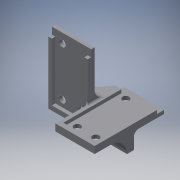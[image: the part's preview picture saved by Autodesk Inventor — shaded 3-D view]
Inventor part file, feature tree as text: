
AUTODESK INVENTOR PART (.ipt)
format: ipt  version: 2016 (Build 200138000, 138)  size: 277,504 bytes
history: native  units: mm
features: extrude x11, sketch x10, projected_geometry x10, fillet x7
ambient origin geometry x8: Origin, YZ Plane, XZ Plane, XY Plane, X Axis, Y Axis, Z Axis, Center Point
bodies: Solid1 (feature_tree)
feature tree (38):
  extrude  "Extrusion1"  Depth=13.0mm
  extrude  "Extrusion4"  Depth=17.0mm
  extrude  "Extrusion8"  Depth=30.0mm TaperAngle=0.0deg
  extrude  "Extrusion14"  Depth=20.0mm TaperAngle=0.0deg
  extrude  "Extrusion15"  Depth=21.0mm
  extrude  "Extrusion16"  Depth=8.0mm
  extrude  "Extrusion18"  Depth=2.8mm
  extrude  "Extrusion19"  Depth=8.0mm
  fillet  "Fillet6"  Radius=3.0mm
  fillet  "Fillet7"  Radius=3.0mm
  fillet  "Fillet8"  Radius=1.5mm
  fillet  "Fillet9"  Radius=1.5mm
  fillet  "Fillet10"  Radius=1.5mm
  fillet  "Fillet11"  Radius=0.6mm
  sketch  "Sketch11"  dims[d22=7.0mm d23=0.0mm d42=20.0mm d43=0.0mm]
  sketch  "Sketch12"  dims[d54=2.7mm d55=21.0mm]
  extrude  "Extrusion11"  Depth=1.5mm
  extrude  "Extrusion12"  Depth=1.0mm
  extrude  "Extrusion13"  Depth=1.0mm
  fillet  "Fillet5"  Radius=1.5mm
  sketch  "Sketch1"  dims[d0=17.0mm d1=13.0mm]
  sketch  "Sketch4"  dims[d2=17.0mm d4=17.0mm]
  projected_geometry  "Projected Loop3"
  sketch  "Sketch8"  dims[d5=14.0mm d6=30.0mm d7=0.0mm]
  projected_geometry  "Projected Loop7"
  projected_geometry  "Projected Loop8"
  projected_geometry  "Projected Loop10"
  projected_geometry  "Projected Loop11"
  sketch  "Sketch13"  dims[d56=3.0mm d57=8.0mm]
  projected_geometry  "Projected Loop12"
  sketch  "Sketch14"  dims[d58=3.0mm d59=2.8mm]
  projected_geometry  "Projected Loop13"
  sketch  "Sketch15"  dims[d60=21.0mm d61=8.0mm d62=3.0mm d63=3.0mm d64=1.5mm d65=0.0mm d66=1.5mm d67=0.0mm d68=1.5mm d69=0.0mm d70=0.6mm]
  projected_geometry  "Projected Loop14"
  sketch  "Sketch16"  dims[d72=3.0mm d80=1.5mm]
  projected_geometry  "Projected Loop15"
  sketch  "Sketch17"  dims[d81=2.0mm d82=25.0mm d83=14.0mm d85=1.5mm d86=0.0mm d87=1.5mm d88=2.0mm d89=25.0mm d91=1.5mm d93=14.0mm d94=1.5mm d95=0.0mm d96=2.9mm d97=21.0mm d98=8.0mm d99=3.0mm d100=3.0mm d101=1.5mm d102=0.0mm d103=3.0mm d104=3.0mm d105=8.0mm d106=21.0mm d107=2.9mm d110=1.5mm d111=0.0mm d112=1.5mm d113=0.0mm d114=20.0mm d115=7.0mm d116=2.0mm d117=4.0mm d118=1.0mm d119=1.0mm]
  projected_geometry  "Projected Loop16"
